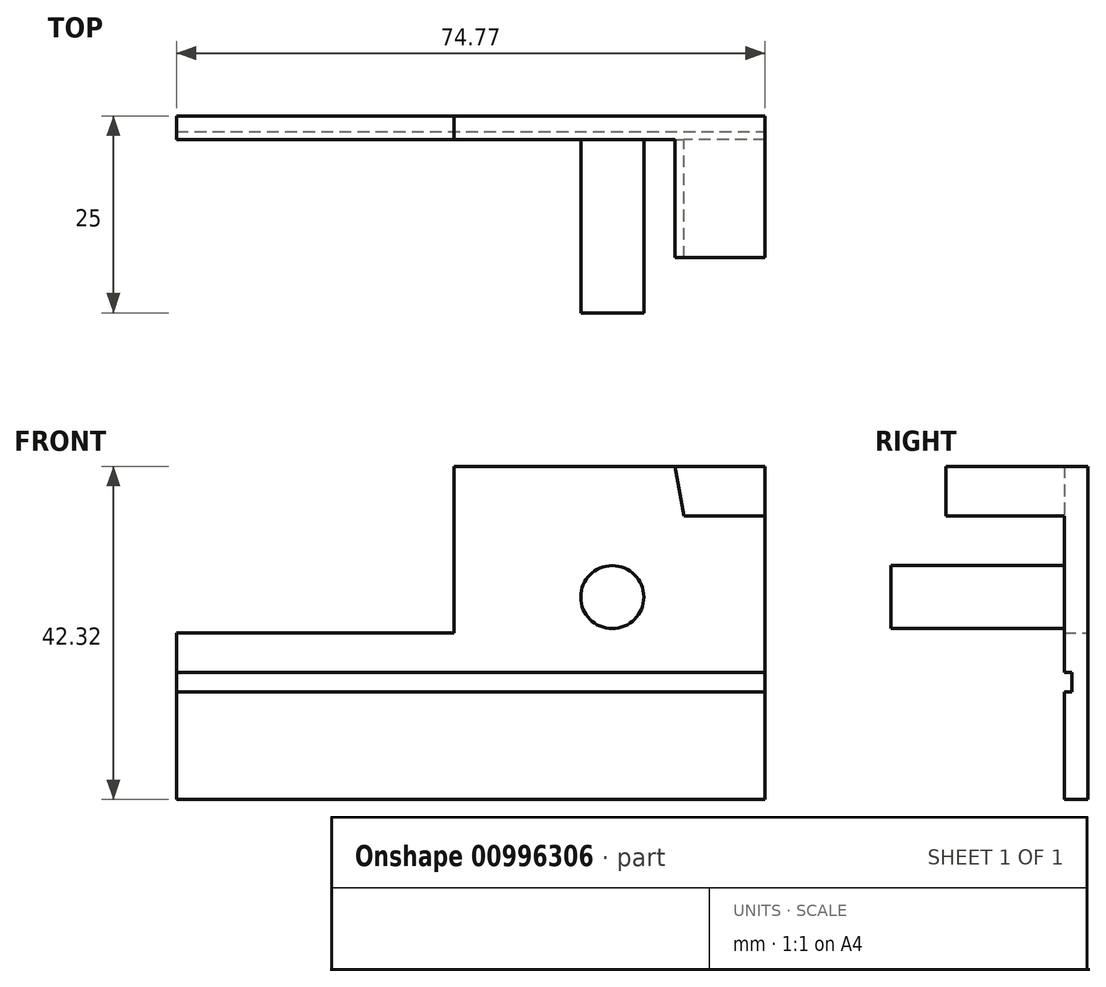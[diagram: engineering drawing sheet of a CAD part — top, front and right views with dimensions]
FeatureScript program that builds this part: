
annotation { "Feature Type Name" : "Feature", "Feature Type Description" : "" }
export const myFeature = defineFeature(function(context is Context, id is Id, definition is map)
    precondition{}
    {
        {
            var Q0;
            Q0=qCreatedBy(makeId("Front.planeOp"),FACE);
            var sketch = newSketch(context, id + "F0", { "sketchPlane" : qUnion([Q0])});
            skLineSegment(sketch, "E0.right", {"start": v(-40.63, 0) * mm, "end": v(-40.63, -21.16) * mm});
            skPoint(sketch, "E0.middle", {"position": v(0, 0) * mm});
            skCircle(sketch, "E1", {"center": v(14.73, 4.55) * mm, "radius": 4 * mm});
            skLineSegment(sketch, "E2", {"start": v(-40.63, 0) * mm, "end": v(-5.38, 0) * mm});
            skLineSegment(sketch, "E3", {"start": v(34.14, 21.16) * mm, "end": v(34.14, -21.16) * mm});
            skLineSegment(sketch, "E4", {"start": v(-5.38, 21.16) * mm, "end": v(-5.38, 0) * mm});
            skLineSegment(sketch, "E5", {"start": v(-5.38, 21.16) * mm, "end": v(34.14, 21.16) * mm});
            skLineSegment(sketch, "E6", {"start": v(-40.63, -21.16) * mm, "end": v(34.14, -21.16) * mm});
            skPoint(sketch, "E7", {"position": v(22.7, 21.16) * mm});
            skLineSegment(sketch, "E8", {"start": v(22.7, 21.16) * mm, "end": v(23.82, 14.88) * mm});
            skLineSegment(sketch, "E9", {"start": v(34.14, 14.88) * mm, "end": v(23.82, 14.88) * mm});
            skSolve(sketch);
        }
        {
            var Q0;
            Q0=makeQuery(id+"F0.imprint","IMPRINT",FACE,{"disambiguationData":[TD([[makeQuery(id+"F0.imprint","IMPRINT",EDGE,{"derivedFrom":sQuery(id+"F0.wireOp",EDGE,"E0.right")}),1.0]])]});
            extrude(context, id + "F1", {"entities" : qUnion([Q0]), "depth" : 3 * mm, "offsetDistance" : 25 * mm});
        }
        {
            var Q0;
            Q0=makeQuery(id+"F0.imprint","IMPRINT",FACE,{"disambiguationData":[TD([[makeQuery(id+"F0.imprint","IMPRINT",EDGE,{"derivedFrom":sQuery(id+"F0.wireOp",EDGE,"E1")}),1.0]])]});
            extrude(context, id + "F2", {"entities" : qUnion([Q0]), "operationType" : NewBodyOperationType.ADD, "depth" : 25 * mm, "offsetDistance" : 25 * mm});
        }
        {
            var Q0;
            Q0=makeQuery(id+"F1.opExtrude","CAP_FACE",FACE,{"disambiguationData":[OSD([sQuery(id+"F0.wireOp",EDGE,"E0.bottom"),sQuery(id+"F0.wireOp",EDGE,"E0.top"),sQuery(id+"F0.wireOp",EDGE,"E0.left"),sQuery(id+"F0.wireOp",EDGE,"E0.right"),sQuery(id+"F0.wireOp",EDGE,"E1"),sQuery(id+"F0.wireOp",EDGE,"azOS4Y7t-rbFC-6Jgf-PcqK-hzSZx8ItXMkZ"),sQuery(id+"F0.wireOp",EDGE,"dh2zZyKk-XKKw-mDZL-l9D1-pIZsX1Tbffab")])],"isStart":false});
            var sketch = newSketch(context, id + "F3", { "sketchPlane" : qUnion([Q0])});
            skLineSegment(sketch, "E10", {"start": v(-40.63, -5) * mm, "end": v(34.14, -5) * mm});
            skLineSegment(sketch, "E11", {"start": v(34.14, -7.5) * mm, "end": v(-40.63, -7.5) * mm});
            skSolve(sketch);
        }
        {
            var Q0;
            {var subQ0=sQuery(id+"F3.wireOp",EDGE,"E10");Q0=makeQuery(id+"F3.imprint","IMPRINT",FACE,{"disambiguationData":[TD([[makeQuery(id+"F3.imprint","IMPRINT",EDGE,{"derivedFrom":subQ0}),-1.0]])]});}
            extrude(context, id + "F4", {"entities" : qUnion([Q0]), "operationType" : NewBodyOperationType.REMOVE, "oppositeDirection" : true, "depth" : 1 * mm, "offsetDistance" : 25 * mm});
        }
        {
            var Q0;
            {var subQ4=sQuery(id+"F0.wireOp",EDGE,"E8");Q0=makeQuery(id+"F0.imprint","IMPRINT",FACE,{"disambiguationData":[TD([[makeQuery(id+"F0.imprint","IMPRINT",EDGE,{"derivedFrom":subQ4}),1.0]])]});}
            extrude(context, id + "F5", {"entities" : qUnion([Q0]), "operationType" : NewBodyOperationType.ADD, "depth" : 18 * mm, "offsetDistance" : 25 * mm});
        }
    });
